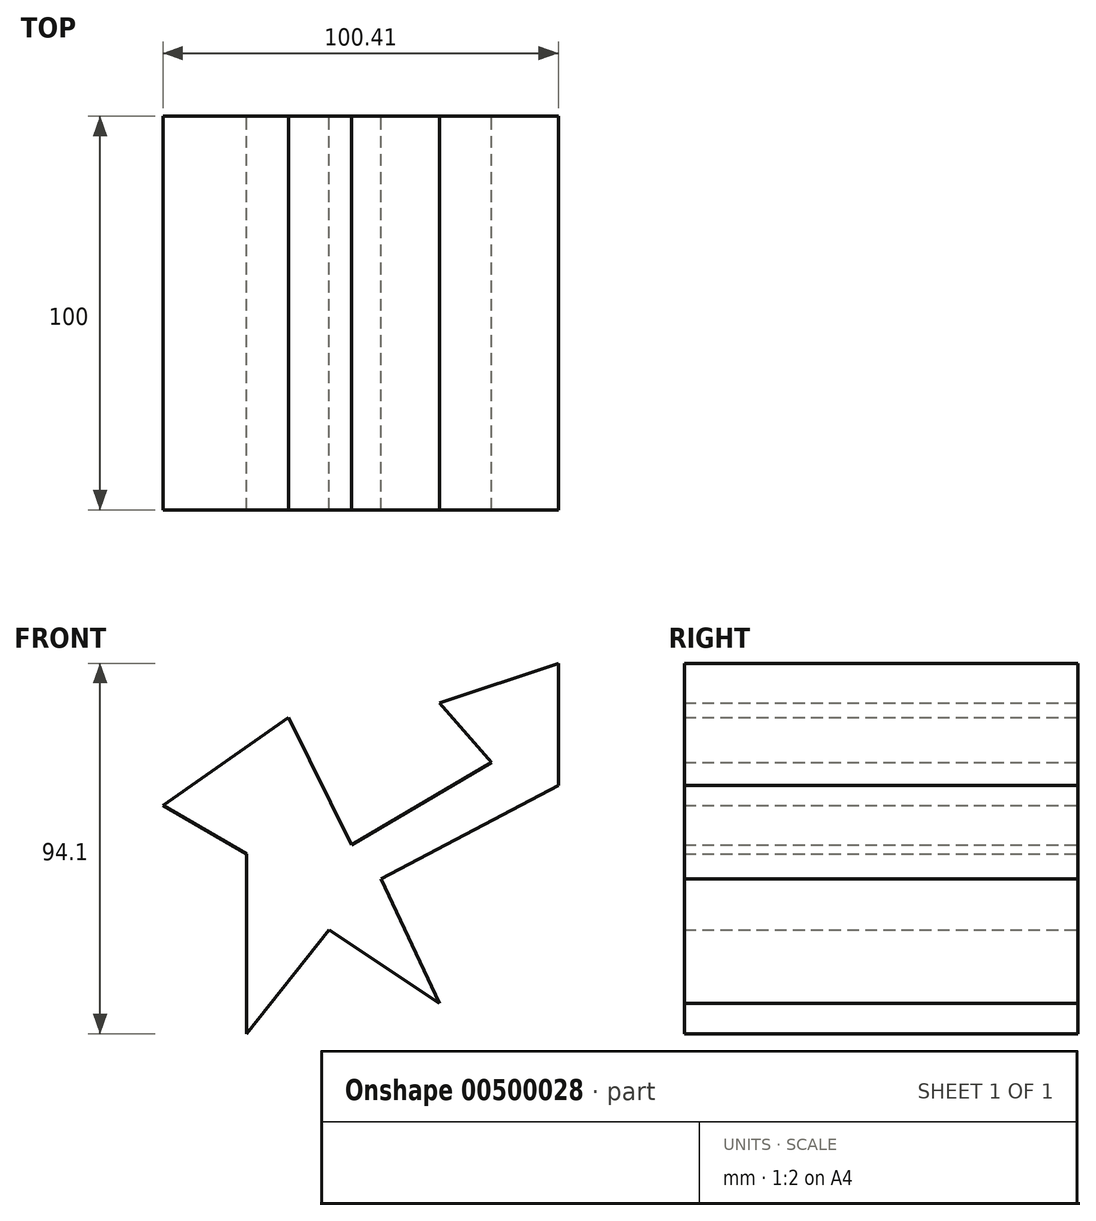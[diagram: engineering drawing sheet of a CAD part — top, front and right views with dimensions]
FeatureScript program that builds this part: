
annotation { "Feature Type Name" : "Feature", "Feature Type Description" : "" }
export const myFeature = defineFeature(function(context is Context, id is Id, definition is map)
    precondition{}
    {
        {
            var Q0;
            Q0=qCreatedBy(makeId("Front.planeOp"),FACE);
            var sketch = newSketch(context, id + "F0", { "sketchPlane" : qUnion([Q0])});
            skLineSegment(sketch, "E0", {"start": v(-55.37, 23.1) * mm, "end": v(-23.52, 45.47) * mm});
            skLineSegment(sketch, "E1", {"start": v(-23.52, 45.47) * mm, "end": v(-7.46, 13.05) * mm});
            skLineSegment(sketch, "E2", {"start": v(-7.46, 13.05) * mm, "end": v(28.11, 34) * mm});
            skLineSegment(sketch, "E3", {"start": v(28.11, 34) * mm, "end": v(14.92, 49.2) * mm});
            skLineSegment(sketch, "E4", {"start": v(14.92, 49.2) * mm, "end": v(45.04, 59.24) * mm});
            skLineSegment(sketch, "E5", {"start": v(45.04, 59.24) * mm, "end": v(45.04, 28.26) * mm});
            skLineSegment(sketch, "E6", {"start": v(45.04, 28.26) * mm, "end": v(0, 4.45) * mm});
            skLineSegment(sketch, "E7", {"start": v(0, 4.45) * mm, "end": v(14.92, -27.11) * mm});
            skLineSegment(sketch, "E8", {"start": v(14.92, -27.11) * mm, "end": v(-13.2, -8.46) * mm});
            skLineSegment(sketch, "E9", {"start": v(-13.2, -8.46) * mm, "end": v(-34.14, -34.86) * mm});
            skLineSegment(sketch, "E10", {"start": v(-34.14, -34.86) * mm, "end": v(-34.14, -5.02) * mm});
            skLineSegment(sketch, "E11", {"start": v(-34.14, -5.02) * mm, "end": v(-34.14, 10.76) * mm});
            skLineSegment(sketch, "E12", {"start": v(-34.14, 10.76) * mm, "end": v(-55.37, 23.1) * mm});
            skSolve(sketch);
        }
        {
            var Q0;
            Q0=makeQuery(id+"F0.imprint","IMPRINT",FACE,{"disambiguationData":[TD([[makeQuery(id+"F0.imprint","IMPRINT",EDGE,{"derivedFrom":sQuery(id+"F0.wireOp",EDGE,"E0")}),-1.0]])]});
            extrude(context, id + "F1", {"entities" : qUnion([Q0]), "endBound" : BoundingType.SYMMETRIC, "depth" : 100 * mm});
        }
    });
